# Revit family: Gira_104600
name_source: partatom
category: Elektroinstallationen
revit_build: Autodesk Revit 2017 (Build: 20160225_1515(x64)
units: mm (PartAtom-declared; Revit-internal decimal feet)

## family parameters
Basisbauteil = Fläche
Beim Laden mit Abzugskörper schneiden = Nein
Bemaßung runder Anschluss = Durchmesser verwenden
Beschriftungsausrichtung beibehalten = Nein
Gemeinsam genutzt = Nein
Raumberechnungspunkt = Nein
Teiletyp = Normal

## types (1)
- Schaltaktor 8f 16 A Hand + Strom C-Last KNX REG
    Andere Bussysteme = ohne
    Anzahl der integrierten Drosseln = 0
    BIM = https://media.stage.bim.site 16f.rfa
    BIMSITE_PRODUCT_ID = a3e6c1ae2a3f1c518e88d64d5e62ebf619d153d8
    Bemessungsstrom = 16 A
    Beschreibung = KNX Schaltaktor 8fach 16 A mit Handbetätigung und Strommessung für C-Lasten  REG plus REG-Schaltaktoren mit integrierter Busankopplung. Zum Schalten von unabhängig ansteuerbaren Lastgruppen. Mit Handschalter zur Umschaltung des Relais (Ein Aus) parallel bzw. ohne KNX Betrieb. Anschluss mehrphasig. Keine zusätzliche Spannungsversorgung erforderlich.  Merkmale:  Handbetätigung der Relais unabhängig vom Bus bzw. der Schaltstellungsanzeige.  Schließer- oder Öffnerbetrieb.  Zentrale Schaltfunktion.  Sammelrückmeldung zur Reduzierung der Buslast.  Aktive oder passive (Objekt auslesbar) zyklische Rückmeldefunktion.  Rückmeldungen lassen sich nach Busspannungswiederkehr verzögern.  Logische Verknüpfungsfunktion für jeden Ausgang.  Sperrfunktion für jeden Kanal parametrierbar. Alternativ Zwangsstellungsfunktion für jeden Ausgang.  Zeitfunktionen (Ein- bzw. Ausschaltverzögerung, Treppenlichtfunktion - auch mit Vorwarnfunktion).  Einbeziehung in Lichtszenen möglich, max. acht interne Szenen je Kanal sind parametrierbar.  Speicherfunktion für Lichtszenen.  Betriebsstundenzähler als Vorwärts- Rückwärtszähler mit Grenzwertfunktion (Grenzwert über Bus veränderbar) für jeden Ausgang aktivierbar.  Eingangsüberwachung auf zyklische Aktualisierung mit Sicherheitsstellung.  Reaktionen bei Busspannungsausfall und -wiederkehr und nach einem ETS-Programmiervorgang für jeden Kanal einstellbar.  Die Schaltkontakte des Schaltaktor 8fach C-Last sind speziell für Lasten mit kapazitivem Charakter und dadurch bedingten kurzzeitigen hohen Einschaltströmen ausgelegt (siehe technische Daten).  Der Schaltaktor besitzt eine integrierte Stromerkennung.  Für jeden Kanal kann eine Strommessung erfolgen.  Stromerkennung: Messung des Laststroms für jeden Kanal.  Schwellwerte zur Lastüberwachung (z. B. Meldung Lastausfall).  Unabhängiges Schalten der acht Ausgänge.  Hinweise :  Montage auf DIN-Hutschiene.  VDE-Zulassung gemäß EN 60669-1, EN 60669-2-1.
    Breite in Teilungseinheiten = 8
    Busspannung pufferbar = Nein
    Bussystem Funkbus = Nein
    Bussystem KNX = Ja
    Bussystem KNX-Funk = Nein
    Bussystem LON = Nein
    Bussystem Powernet = Nein
    Datenblatt = https://media.stage.bim.site
    Datenblatt 1 = https://media.stage.bim.site
    GTIN = 4010337042273
    Geeignet für C-Last = Ja
    HAN = 104600
    HeinzeBIM = https://www.heinze.de
    Hersteller = Gira
    Kosten = 0 $
    Max. Anzahl der Schaltausgänge = 8
    Max. Ausgangsstrom = 0 A
    Mit Busankopplung = Ja
    Mit LED-Anzeige = Nein
    Montageart = REG
    Produktseite = https://media.stage.bim.site
    Typname = Schaltaktor 8f 16 A Hand + Strom C-Last KNX REG
    URL = https://www.gira.de
    Vor Ort-/Handbedienung = Ja
    Vorgabe-Ansicht = 1219 mm

## geometry (parser evidence)
native form markers: Sweep x3
no freeform markers — native parametric forms only
